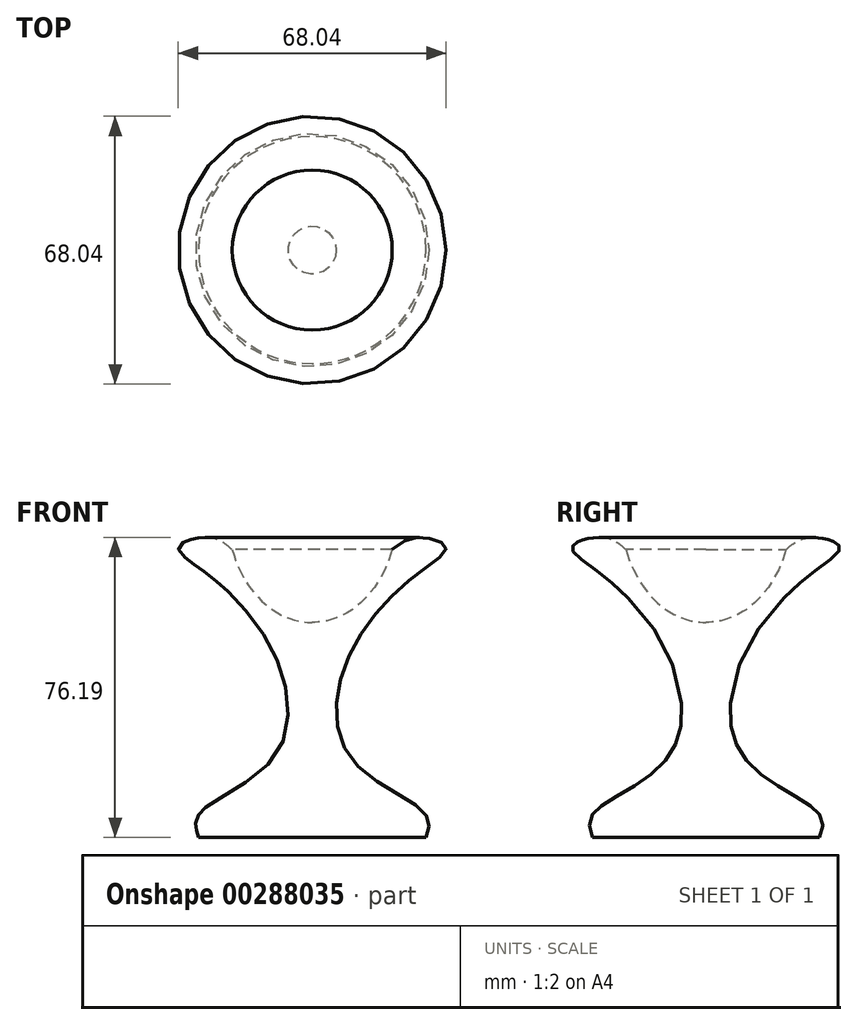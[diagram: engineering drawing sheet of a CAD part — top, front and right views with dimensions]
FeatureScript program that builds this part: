
annotation { "Feature Type Name" : "Feature", "Feature Type Description" : "" }
export const myFeature = defineFeature(function(context is Context, id is Id, definition is map)
    precondition{}
    {
        {
            var Q0;
            Q0=qCreatedBy(makeId("Front.planeOp"),FACE);
            var sketch = newSketch(context, id + "F0", { "sketchPlane" : qUnion([Q0])});
            skLineSegment(sketch, "E0", {"start": v(0, -36.89) * mm, "end": v(-28.87, -36.89) * mm});
            skEllipticalArc(sketch, "E1", {});
            skFitSpline(sketch, "E2", {"points": [v(-20.32, 36.21) * mm, v(-28.34, 39.25) * mm, v(-34, 36.82) * mm, v(-26.33, 29.76) * mm, v(-8.77, 7.76) * mm, v(-10.18, -17.26) * mm, v(-28.87, -31.06) * mm, v(-28.87, -36.89) * mm], "startDerivative": vector(-73.27, 69.56) * mm, "endDerivative": vector(22.71, -61.93) * mm});
            skLineSegment(sketch, "E3", {"start": v(0, 43.63) * mm, "end": v(0, -36.89) * mm, "construction": true});
            skLineSegment(sketch, "E4", {"start": v(0, 17.7) * mm, "end": v(0, -36.89) * mm});
            const initialGuessF0  = {"E1": [0, 0.04564482718706131, 0, -1, 0.02794, 0.02159, 5.056766944238978, 0]};
            skSetInitialGuess(sketch, initialGuessF0);
            skSolve(sketch);
        }
        {
            var Q0;
            Q0=makeQuery(id+"F0.imprint","IMPRINT",FACE,{"disambiguationData":[TD([[makeQuery(id+"F0.imprint","IMPRINT",EDGE,{"derivedFrom":sQuery(id+"F0.wireOp",EDGE,"E0")}),-1.0]])]});
            var Q1;
            Q1=sQuery(id+"F0.wireOp",EDGE,"E3");
            revolve(context, id + "F1", {"entities" : qUnion([Q0]), "axis" : qUnion([Q1]), "revolveType" : RevolveType.FULL});
        }
    });
